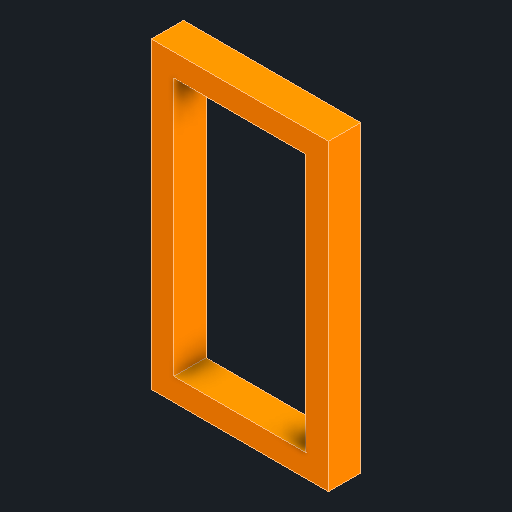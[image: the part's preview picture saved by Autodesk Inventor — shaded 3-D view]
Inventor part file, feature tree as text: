
AUTODESK INVENTOR PART (.ipt)
format: ipt  version: 2023.4 (Build 274418000, 418)  size: 117,760 bytes
history: native  units: mm
features: other x3, plane x1, extrude x1, reference x1
ambient origin geometry x8: Origin, YZ Plane, XZ Plane, XY Plane, X Axis, Y Axis, Z Axis, Center Point
bodies: Solid1 (feature_tree)
feature tree (6):
  plane  "Work Plane1"
  extrude  "Extrusion1"  Depth=0.25mm
  reference  "Reference1"
  other  "Cube V1-2.iam"
  other  "Sample Holder:1"
  other  "Cube 1x1 V2.iam"
